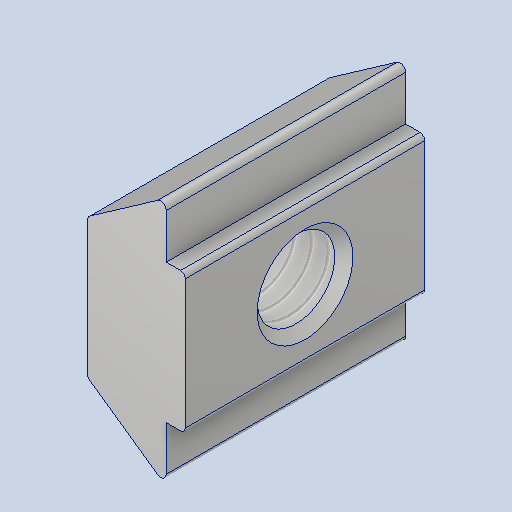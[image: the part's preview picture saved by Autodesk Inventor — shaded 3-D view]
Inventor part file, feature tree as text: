
AUTODESK INVENTOR PART (.ipt)
format: ipt  version: 2024 (Build 280153000, 153)  size: 175,104 bytes
history: native  units: mm
features: other x28, sketch x2, extrude x1, revolve x1, thread x1
ambient origin geometry x8: Origin, YZ Plane, XZ Plane, XY Plane, X Axis, Y Axis, Z Axis, Center Point
bodies: Solid1 (feature_tree)
feature tree (33):
  extrude  "Extrusion1"  TaperAngle=360.0deg  [1 undecoded]
  revolve  "Revolution1"  [1 undecoded]
  thread  "Thread1"  [1 undecoded]
  other  "nut_XY"
  other  "nut_YZ"
  other  "nut_ZX"
  other  "nut_X"
  other  "nut_Y"
  other  "nut_Z"
  other  "nut_Center"
  other  "to_bolt_XY"
  other  "to_bolt_YZ"
  other  "to_bolt_ZX"
  other  "to_bolt_X"
  other  "to_bolt_Y"
  other  "to_bolt_Z"
  other  "to_bolt_Center"
  other  "to_frames_XY"
  other  "to_frames_YZ"
  other  "to_frames_ZX"
  other  "to_frames_X"
  other  "to_frames_Y"
  other  "to_frames_Z"
  other  "to_frames_Center"
  other  "to_lane_XY"
  other  "to_lane_YZ"
  other  "to_lane_ZX"
  other  "to_lane_X"
  other  "to_lane_Y"
  other  "to_lane_Z"
  other  "to_lane_Center"
  sketch  "Sketch_2"  dims[d0=10.0mm d1=0.0mm d2=360.0deg]
  sketch  "Sketch_5"  dims[d3=3.342mm d4=0.0mm d5=0.0mm d6=0.0mm]
note: 3 required parameter values undecoded (feature->parameter linkage not recoverable at this tier; creation-order binding heuristic only, values carry confidence <= 0.55)